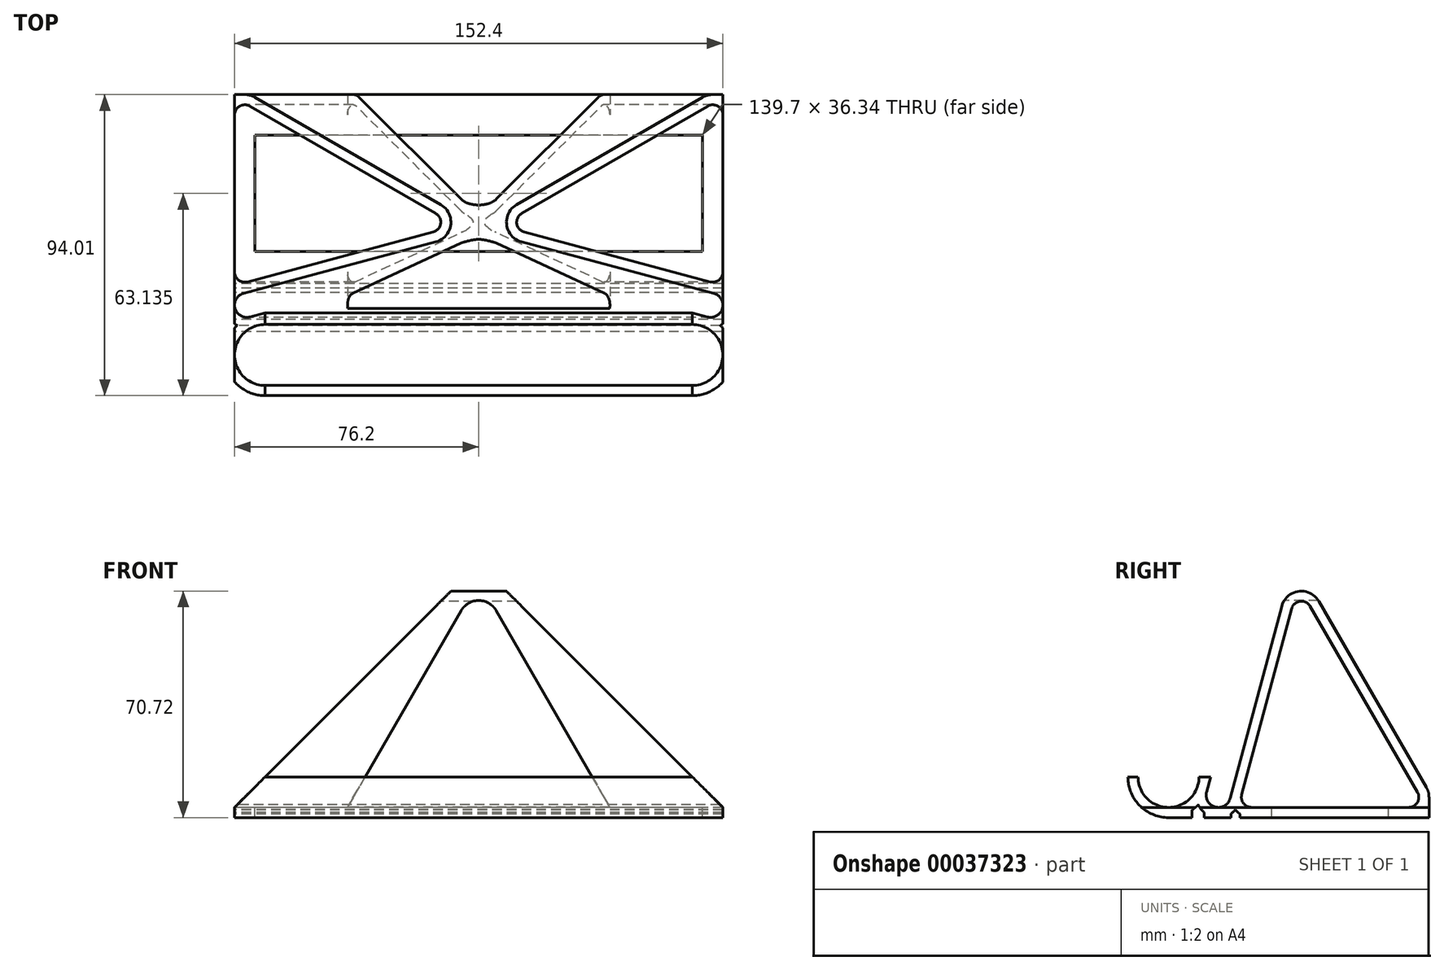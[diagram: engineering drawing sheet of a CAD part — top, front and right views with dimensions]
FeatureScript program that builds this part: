
annotation { "Feature Type Name" : "Feature", "Feature Type Description" : "" }
export const myFeature = defineFeature(function(context is Context, id is Id, definition is map)
    precondition{}
    {
        {
            var Q0;
            Q0=qCreatedBy(makeId("Right.planeOp"),FACE);
            var sketch = newSketch(context, id + "F0", { "sketchPlane" : qUnion([Q0])});
            skArc(sketch, "E0", {"start": v(-19.27, 12.7) * mm, "mid": v(-9.75, 3.18) * mm, "end": v(-0.22, 12.7) * mm});
            skArc(sketch, "E1", {"start": v(-22.45, 12.7) * mm, "mid": v(-18.73, 3.72) * mm, "end": v(-9.75, 0) * mm});
            skLineSegment(sketch, "E2", {"start": v(-22.45, 12.7) * mm, "end": v(-19.27, 12.7) * mm});
            skLineSegment(sketch, "E3", {"start": v(71.56, 0) * mm, "end": v(16.16, 0) * mm});
            skPoint(sketch, "E4.orphan", {"position": v(-36.1, 12.7) * mm});
            skLineSegment(sketch, "E5.trimOffspring", {"start": v(-0.22, 12.7) * mm, "end": v(3.4, 12.7) * mm});
            skLineSegment(sketch, "E6", {"start": v(2.14, 7.97) * mm, "end": v(11.28, 42.11) * mm});
            skArc(sketch, "E7", {"start": v(2.14, 7.97) * mm, "mid": v(4.83, 3.3) * mm, "end": v(9.5, 6) * mm});
            skLineSegment(sketch, "E8", {"start": v(9.5, 6) * mm, "end": v(25.58, 66.01) * mm});
            skLineSegment(sketch, "E9", {"start": v(37.2, 67.54) * mm, "end": v(70.7, 9.52) * mm});
            skLineSegment(sketch, "E10", {"start": v(5.82, 6.98) * mm, "end": v(71.56, 252.33) * mm, "construction": true});
            skLineSegment(sketch, "E11.0", {"start": v(65.2, 3.18) * mm, "end": v(16.16, 3.17) * mm});
            skLineSegment(sketch, "E11.1", {"start": v(34.46, 65.95) * mm, "end": v(67.96, 7.94) * mm});
            skLineSegment(sketch, "E11.2", {"start": v(13.1, 7.17) * mm, "end": v(28.64, 65.19) * mm});
            skPoint(sketch, "E12.visualSharp", {"position": v(29.54, 80.82) * mm});
            skArc(sketch, "E12.filletArc", {"start": v(37.2, 67.54) * mm, "mid": v(30.88, 70.66) * mm, "end": v(25.58, 66.01) * mm});
            skPoint(sketch, "E13.visualSharp", {"position": v(30.63, 72.6) * mm});
            skArc(sketch, "E13.filletArc", {"start": v(34.46, 65.95) * mm, "mid": v(31.3, 67.51) * mm, "end": v(28.64, 65.19) * mm});
            skPoint(sketch, "E14.visualSharp", {"position": v(12.03, 3.17) * mm});
            skArc(sketch, "E14.filletArc", {"start": v(13.1, 7.17) * mm, "mid": v(13.65, 4.42) * mm, "end": v(16.16, 3.17) * mm});
            skArc(sketch, "E15.filletArc", {"start": v(65.2, 3.17) * mm, "mid": v(67.96, 4.76) * mm, "end": v(67.96, 7.94) * mm});
            skArc(sketch, "E16.0", {"start": v(-0.5, 4) * mm, "mid": v(0.3, 2.7) * mm, "end": v(1.37, 1.6) * mm});
            skArc(sketch, "E17", {"start": v(11.14, 2.46) * mm, "mid": v(11.78, 1.75) * mm, "end": v(12.53, 1.15) * mm});
            skLineSegment(sketch, "E18.trimOffspring", {"start": v(16.16, 0) * mm, "end": v(12.53, 0) * mm});
            skLineSegment(sketch, "E19.left", {"start": v(1.37, 1.6) * mm, "end": v(1.37, 0) * mm});
            skLineSegment(sketch, "E19.right", {"start": v(-2.42, 2.33) * mm, "end": v(-2.42, 0) * mm});
            skLineSegment(sketch, "E20.left", {"start": v(9.75, 1.21) * mm, "end": v(9.75, 0) * mm});
            skLineSegment(sketch, "E20.right", {"start": v(12.53, 1.15) * mm, "end": v(12.53, 0) * mm});
            skArc(sketch, "E21.trimOffspring", {"start": v(-2.42, 2.33) * mm, "mid": v(-1.42, 3.11) * mm, "end": v(-0.5, 4) * mm});
            skLineSegment(sketch, "E22.trimOffspring", {"start": v(-2.42, 0) * mm, "end": v(-9.75, 0) * mm});
            skArc(sketch, "E23.trimOffspring", {"start": v(9.75, 1.21) * mm, "mid": v(10.49, 1.8) * mm, "end": v(11.14, 2.46) * mm});
            skPoint(sketch, "E24.orphan", {"position": v(9.75, 2.46) * mm});
            skLineSegment(sketch, "E25.trimOffspring", {"start": v(16.16, 0) * mm, "end": v(16.16, 0) * mm});
            skLineSegment(sketch, "E26.trimOffspring", {"start": v(9.75, 0) * mm, "end": v(1.37, 0) * mm});
            skLineSegment(sketch, "E27", {"start": v(71.56, 6.35) * mm, "end": v(71.56, 0) * mm});
            skArc(sketch, "E28", {"start": v(71.56, 6.35) * mm, "mid": v(71.34, 8) * mm, "end": v(70.7, 9.53) * mm});
            skPoint(sketch, "E29.orphan", {"position": v(76.2, 0) * mm});
            skSolve(sketch);
        }
        {
            var Q0;
            Q0 = qSketchRegion(id + "F0", true);
            extrude(context, id + "F1", {"entities" : qUnion([Q0]), "depth" : 152.4 * mm, "symmetric" : true});
        }
        {
            var Q0;
            Q0=makeQuery(id+"F1.opExtrude","SWEPT_FACE",FACE,{"disambiguationData":[OSD([sQuery(id+"F0.wireOp",EDGE,"E11.0")])]});
            var sketch = newSketch(context, id + "F2", { "sketchPlane" : qUnion([Q0])});
            skLineSegment(sketch, "E30.0", {"start": v(69.85, 22.51) * mm, "end": v(-69.85, 22.51) * mm});
            skLineSegment(sketch, "E30.1", {"start": v(69.85, 58.86) * mm, "end": v(69.85, 22.51) * mm});
            skLineSegment(sketch, "E30.2", {"start": v(69.85, 58.86) * mm, "end": v(-69.85, 58.86) * mm});
            skLineSegment(sketch, "E30.3", {"start": v(-69.85, 58.86) * mm, "end": v(-69.85, 22.51) * mm});
            skSolve(sketch);
        }
        {
            var Q0;
            Q0 = qSketchRegion(id + "F2", true);
            extrude(context, id + "F3", {"entities" : qUnion([Q0]), "operationType" : NewBodyOperationType.REMOVE, "oppositeDirection" : true, "depth" : 25.4 * mm});
        }
        {
            var Q0;
            Q0=makeQuery(id+"F1.opExtrude","CAP_EDGE",EDGE,{"disambiguationData":[OSD([sQuery(id+"F0.wireOp",EDGE,"E7")])],"isStart":false});
            cPoint(context, id + "F4", {"entities" : qUnion([Q0]), "parameter" : 0.5});
        }
        {
            var Q0;
            Q0=qCreatedBy(makeId("Front.planeOp"),FACE);
            var Q1;
            Q1 = qCreatedBy(id + "F4" ,VERTEX);
            cPlane(context, id + "F5", {"entities" : qUnion([Q0, Q1]), "cplaneType" : CPlaneType.PLANE_POINT, "offset" : 25.4 * mm, "width" : 152.4 * mm, "height" : 152.4 * mm});
        }
        {
            var Q0;
            Q0=qCreatedBy(id+"F5.planeOp",FACE);
            var sketch = newSketch(context, id + "F6", { "sketchPlane" : qUnion([Q0])});
            skLineSegment(sketch, "E31", {"start": v(6.04, 73.34) * mm, "end": v(76.2, 3.17) * mm});
            skLineSegment(sketch, "E32", {"start": v(76.2, 3.17) * mm, "end": v(76.2, 73.34) * mm});
            skLineSegment(sketch, "E33", {"start": v(76.2, 73.34) * mm, "end": v(6.04, 73.34) * mm});
            skLineSegment(sketch, "E34", {"start": v(0, 0) * mm, "end": v(0, -51.47) * mm, "construction": true});
            skLineSegment(sketch, "E35.MirrorCS", {"start": v(-6.04, 73.34) * mm, "end": v(-76.2, 3.17) * mm});
            skLineSegment(sketch, "E36.MirrorCS", {"start": v(-76.2, 73.34) * mm, "end": v(-6.04, 73.34) * mm});
            skLineSegment(sketch, "E37.MirrorCS", {"start": v(-76.2, 3.17) * mm, "end": v(-76.2, 73.34) * mm});
            skSolve(sketch);
        }
        {
            var Q0;
            Q0 = qSketchRegion(id + "F6", true);
            extrude(context, id + "F7", {"entities" : qUnion([Q0]), "operationType" : NewBodyOperationType.REMOVE, "endBound" : BoundingType.THROUGH_ALL, "depth" : 25.4 * mm, "hasSecondDirection" : true, "secondDirectionBound" : BoundingType.THROUGH_ALL, "secondDirectionOppositeDirection" : true, "secondDirectionDepth" : 25.4 * mm});
        }
        {
            var Q0;
            Q0=qCreatedBy(id+"F5.planeOp",FACE);
            var sketch = newSketch(context, id + "F8", { "sketchPlane" : qUnion([Q0])});
            skLineSegment(sketch, "E38", {"start": v(-40.96, 3.17) * mm, "end": v(-5.5, 64.59) * mm});
            skLineSegment(sketch, "E39", {"start": v(0, 0) * mm, "end": v(0, 78.12) * mm, "construction": true});
            skLineSegment(sketch, "E40.MirrorCS", {"start": v(40.96, 3.17) * mm, "end": v(5.5, 64.59) * mm});
            skPoint(sketch, "E41.visualSharp", {"position": v(0, 74.11) * mm});
            skArc(sketch, "E41.filletArc", {"start": v(5.5, 64.59) * mm, "mid": v(0, 67.76) * mm, "end": v(-5.5, 64.59) * mm});
            skLineSegment(sketch, "E42", {"start": v(-40.96, 3.17) * mm, "end": v(40.96, 3.17) * mm});
            skSolve(sketch);
        }
        {
            var Q0;
            Q0 = qSketchRegion(id + "F8", true);
            extrude(context, id + "F9", {"entities" : qUnion([Q0]), "operationType" : NewBodyOperationType.REMOVE, "endBound" : BoundingType.THROUGH_ALL, "oppositeDirection" : true, "depth" : 25.4 * mm});
        }
    });
